# Revit family: Electronics_Expansion-Outputs_Biamp_Vocia_Output-Device_VO-4__
name_source: partatom
category: Communication Devices
units: mm (PartAtom-declared; Revit-internal decimal feet)

## family parameters
Cut with Voids When Loaded = No
Host = Face
Maintain Annotation Orientation = No
OmniClass Number = 23.85.10.11.14
OmniClass Title = Audio Equipment
Part Type = Normal
Room Calculation Point = No
Round Connector Dimension = Use Diameter
Shared = No

## types (1)
- VO-4
    A/D Converters = 24-bit
    Altitude = 0-10,000 ft (0-3000m) MSL
    Apparent Load = 0 VA
    Compliance = FCC Part 15B (USA) ,CE marked (Europe) ,RoHS Directive (Europe)
    Connector Description = PoE 802.3af Class 3
    Crosstalk = > 80dB
    Default Elevation = 48 "
    Depth = 10 "
    Description = Vocia® VO-4 Output Device
    Dynamic Range = >100dB
    Frequency Response = ± 1dB
    Height = 1.75 "
    Housing Material = Biamp - Metal - Silver
    Humidity = 0-95% relative humidity (non-condensing)
    Input Impedance = 100 kohm
    Manufacturer = Biamp
    Max Input Threshold = 10V
    Max Input Voltage = 12V
    Max Operating Voltage = 125V AC, 60V DC
    Max Power Consumption = 0 W
    Max Switching Capacity = 37 VA
    Maximum Load Impedance = 600 kohm
    Maximum Output Level = +22dBu
    Maximum Output Load = 2 kohm
    Min Input Threshold = 150mV
    Min Operating Load = 10µA 10mV DC
    Model = Vocia VO-4
    Network Connection = RJ45 with shielded Ethernet (CAT5, CAT5e, CAT6, or CAT 7)
    Nominal Output Level = -10dBu, 0dBu, +4dBu (selectable)
    Number of Poles = 1
    Power Factor = 1
    Product Documentation Link = https://downloads.biamp.com
    Product Page URL = https://www.biamp.com
    Product data url = https://www.bimobject.com
    Sample Rate = 48kHz
    THD+N = <0.02%
    Temperature Range = 23 - 104° F (-8 - 42° C)
    Type Control Inputs = Digital, variable threshold
    Type Control Outputs = Single Form C voltage free change over contact
    URL = https://www.biamp.com
    Vocia VO-4 = Yes
    Voltage = 0 V
    Weight = 6.40 lbf
    Width = 19 "

## geometry (parser evidence)
native form markers: Sweep x2
no freeform markers — native parametric forms only
